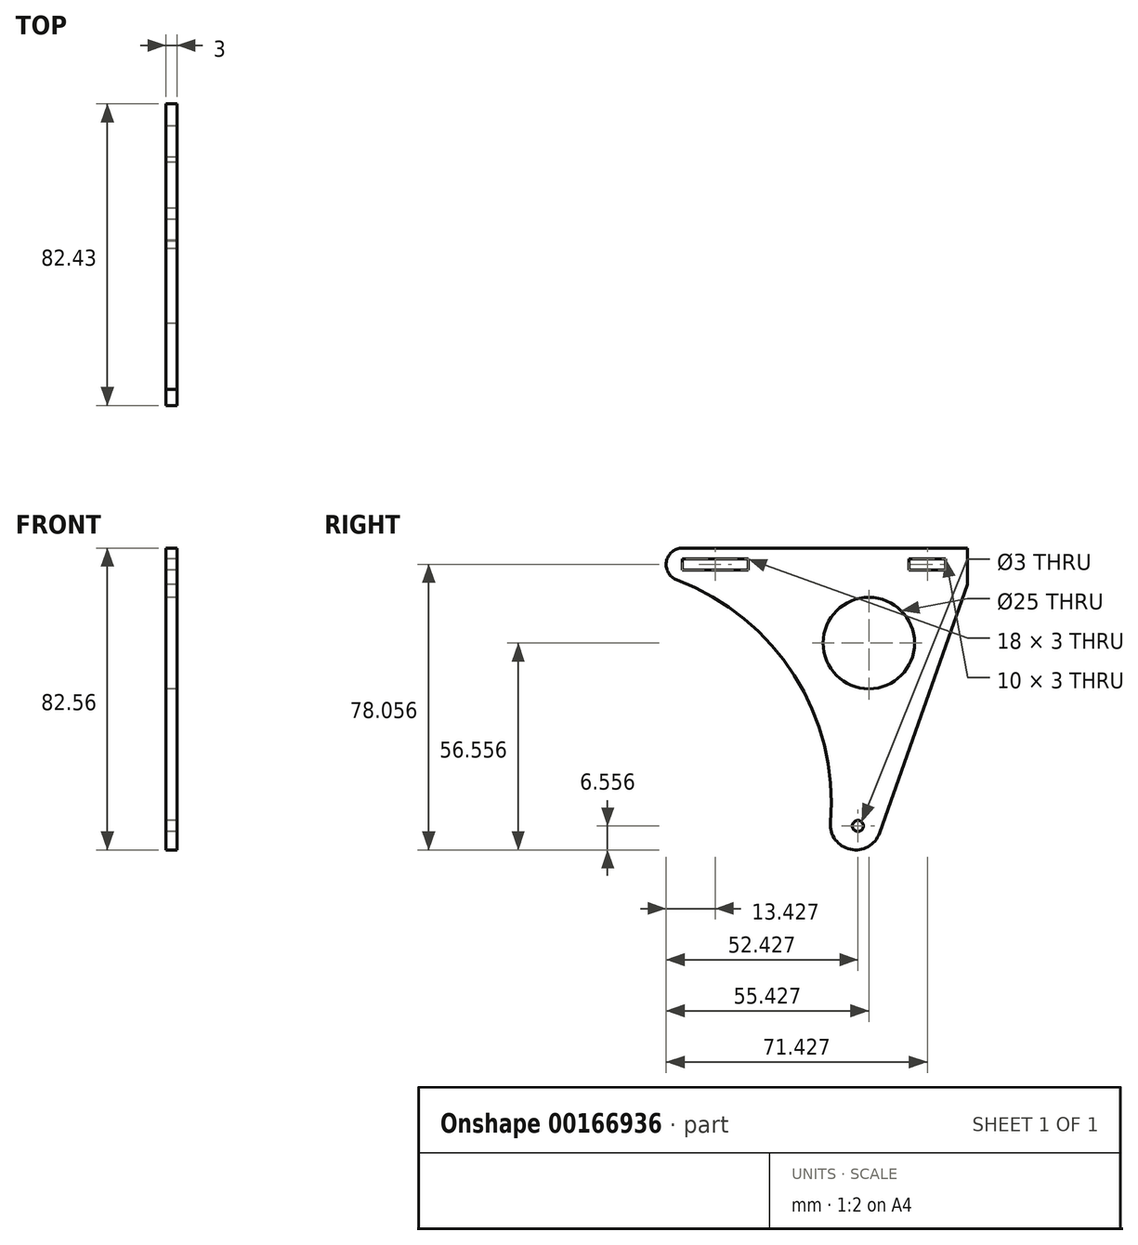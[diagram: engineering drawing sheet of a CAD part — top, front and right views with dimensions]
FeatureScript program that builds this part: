
annotation { "Feature Type Name" : "Feature", "Feature Type Description" : "" }
export const myFeature = defineFeature(function(context is Context, id is Id, definition is map)
    precondition{}
    {
        {
            var Q0;
            Q0=qCreatedBy(makeId("Right.planeOp"),FACE);
            var sketch = newSketch(context, id + "F0", { "sketchPlane" : qUnion([Q0])});
            skLineSegment(sketch, "E0", {"start": v(19.4, -12.72) * mm, "end": v(9.4, -12.72) * mm});
            skLineSegment(sketch, "E1", {"start": v(9.4, -12.72) * mm, "end": v(9.4, -9.72) * mm});
            skLineSegment(sketch, "E2", {"start": v(9.4, -9.72) * mm, "end": v(19.4, -9.72) * mm});
            skLineSegment(sketch, "E3", {"start": v(19.4, -9.72) * mm, "end": v(19.4, -12.72) * mm});
            skCircle(sketch, "E4", {"center": v(-1.6, -32.72) * mm, "radius": 12.5 * mm});
            skLineSegment(sketch, "E5", {"start": v(-52.6, -9.72) * mm, "end": v(-52.6, -12.72) * mm});
            skLineSegment(sketch, "E6", {"start": v(-52.6, -12.72) * mm, "end": v(-34.6, -12.72) * mm});
            skLineSegment(sketch, "E7", {"start": v(-34.6, -12.72) * mm, "end": v(-34.6, -9.72) * mm});
            skLineSegment(sketch, "E8", {"start": v(-34.6, -9.72) * mm, "end": v(-52.6, -9.72) * mm});
            skCircle(sketch, "E9", {"center": v(-4.6, -82.72) * mm, "radius": 1.5 * mm});
            skLineSegment(sketch, "E10", {"start": v(25.4, -16.72) * mm, "end": v(1.31, -84.67) * mm});
            skArc(sketch, "E11", {"start": v(1.31, -84.67) * mm, "mid": v(-6.67, -89.12) * mm, "end": v(-12.1, -81.78) * mm});
            skArc(sketch, "E12", {"start": v(-12.1, -81.78) * mm, "mid": v(-21.95, -41.56) * mm, "end": v(-54.1, -15.46) * mm});
            skArc(sketch, "E13", {"start": v(-54.1, -15.46) * mm, "mid": v(-56.96, -10.48) * mm, "end": v(-52.6, -6.72) * mm});
            skLineSegment(sketch, "E14", {"start": v(-52.6, -6.72) * mm, "end": v(25.4, -6.72) * mm});
            skLineSegment(sketch, "E15", {"start": v(25.4, -6.72) * mm, "end": v(25.4, -16.72) * mm});
            skSolve(sketch);
        }
        {
            var Q0;
            Q0=makeQuery(id+"F0.imprint","IMPRINT",FACE,{"disambiguationData":[TD([[makeQuery(id+"F0.imprint","IMPRINT",EDGE,{"derivedFrom":sQuery(id+"F0.wireOp",EDGE,"E0")}),1.0]])]});
            extrude(context, id + "F1", {"entities" : qUnion([Q0]), "endBound" : BoundingType.SYMMETRIC, "depth" : 3 * mm});
        }
    });
